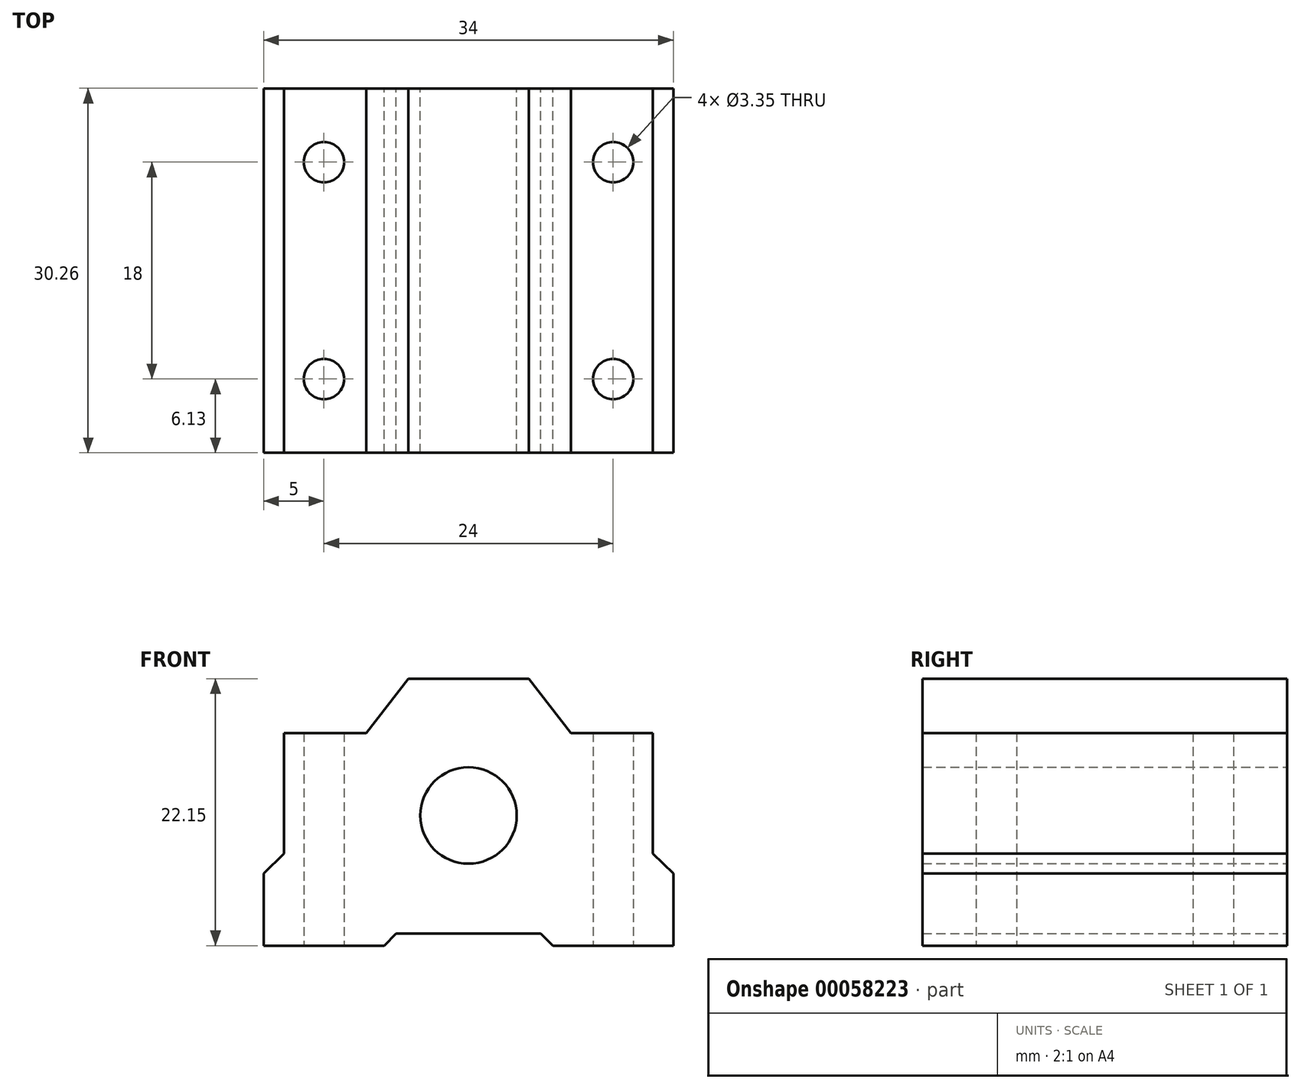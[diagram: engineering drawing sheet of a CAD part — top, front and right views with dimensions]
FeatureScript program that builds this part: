
annotation { "Feature Type Name" : "Feature", "Feature Type Description" : "" }
export const myFeature = defineFeature(function(context is Context, id is Id, definition is map)
    precondition{}
    {
        {
            var Q0;
            Q0=qCreatedBy(makeId("Front.planeOp"),FACE);
            var sketch = newSketch(context, id + "F0", { "sketchPlane" : qUnion([Q0])});
            skCircle(sketch, "E0", {"center": v(0, 0) * mm, "radius": 4 * mm});
            skLineSegment(sketch, "E1", {"start": v(0, 0) * mm, "end": v(0, 28.54) * mm, "construction": true});
            skLineSegment(sketch, "E2", {"start": v(-5, 11.35) * mm, "end": v(-8.5, 6.85) * mm});
            skLineSegment(sketch, "E3", {"start": v(-8.5, 6.85) * mm, "end": v(-15.3, 6.85) * mm});
            skLineSegment(sketch, "E4", {"start": v(-15.3, 6.85) * mm, "end": v(-15.3, -3.15) * mm});
            skLineSegment(sketch, "E5", {"start": v(-15.3, -3.15) * mm, "end": v(-17, -4.8) * mm});
            skLineSegment(sketch, "E6", {"start": v(-17, -4.8) * mm, "end": v(-17, -10.8) * mm});
            skLineSegment(sketch, "E7", {"start": v(-17, -10.8) * mm, "end": v(-7, -10.8) * mm});
            skLineSegment(sketch, "E8", {"start": v(-7, -10.8) * mm, "end": v(-6, -9.8) * mm});
            skLineSegment(sketch, "E9.MirrorCS", {"start": v(7, -10.8) * mm, "end": v(6, -9.8) * mm});
            skLineSegment(sketch, "E10.MirrorCS", {"start": v(17, -10.8) * mm, "end": v(7, -10.8) * mm});
            skLineSegment(sketch, "E11.MirrorCS", {"start": v(17, -4.8) * mm, "end": v(17, -10.8) * mm});
            skLineSegment(sketch, "E12.MirrorCS", {"start": v(15.3, -3.15) * mm, "end": v(17, -4.8) * mm});
            skLineSegment(sketch, "E13.MirrorCS", {"start": v(15.3, 6.85) * mm, "end": v(15.3, -3.15) * mm});
            skLineSegment(sketch, "E14.MirrorCS", {"start": v(8.5, 6.85) * mm, "end": v(15.3, 6.85) * mm});
            skLineSegment(sketch, "E15.MirrorCS", {"start": v(5, 11.35) * mm, "end": v(8.5, 6.85) * mm});
            skLineSegment(sketch, "E16", {"start": v(-5, 11.35) * mm, "end": v(5, 11.35) * mm});
            skLineSegment(sketch, "E17", {"start": v(-6, -9.8) * mm, "end": v(6, -9.8) * mm});
            skSolve(sketch);
        }
        {
            var Q0;
            Q0 = qSketchRegion(id + "F0", true);
            extrude(context, id + "F1", {"entities" : qUnion([Q0]), "depth" : 30.25 * mm, "symmetric" : true});
        }
        {
            var Q0;
            Q0=makeQuery(id+"F1.opExtrude","SWEPT_FACE",FACE,{"disambiguationData":[OSD([sQuery(id+"F0.wireOp",EDGE,"E7")])]});
            var sketch = newSketch(context, id + "F2", { "sketchPlane" : qUnion([Q0])});
            skLineSegment(sketch, "E18", {"start": v(0, 0) * mm, "end": v(0, 27.72) * mm, "construction": true});
            skCircle(sketch, "E19", {"center": v(-12, 9) * mm, "radius": 1.67 * mm});
            skLineSegment(sketch, "E20", {"start": v(0, 0) * mm, "end": v(-30.82, 0) * mm, "construction": true});
            skCircle(sketch, "E21.MirrorC", {"center": v(12, 9) * mm, "radius": 1.67 * mm});
            skCircle(sketch, "E22.MirrorC", {"center": v(-12, -9) * mm, "radius": 1.67 * mm});
            skCircle(sketch, "E23.MirrorC", {"center": v(12, -9) * mm, "radius": 1.67 * mm});
            skSolve(sketch);
        }
        {
            var Q0;
            Q0 = qSketchRegion(id + "F2", true);
            extrude(context, id + "F3", {"entities" : qUnion([Q0]), "operationType" : NewBodyOperationType.REMOVE, "endBound" : BoundingType.THROUGH_ALL, "oppositeDirection" : true, "depth" : 25 * mm});
        }
    });
